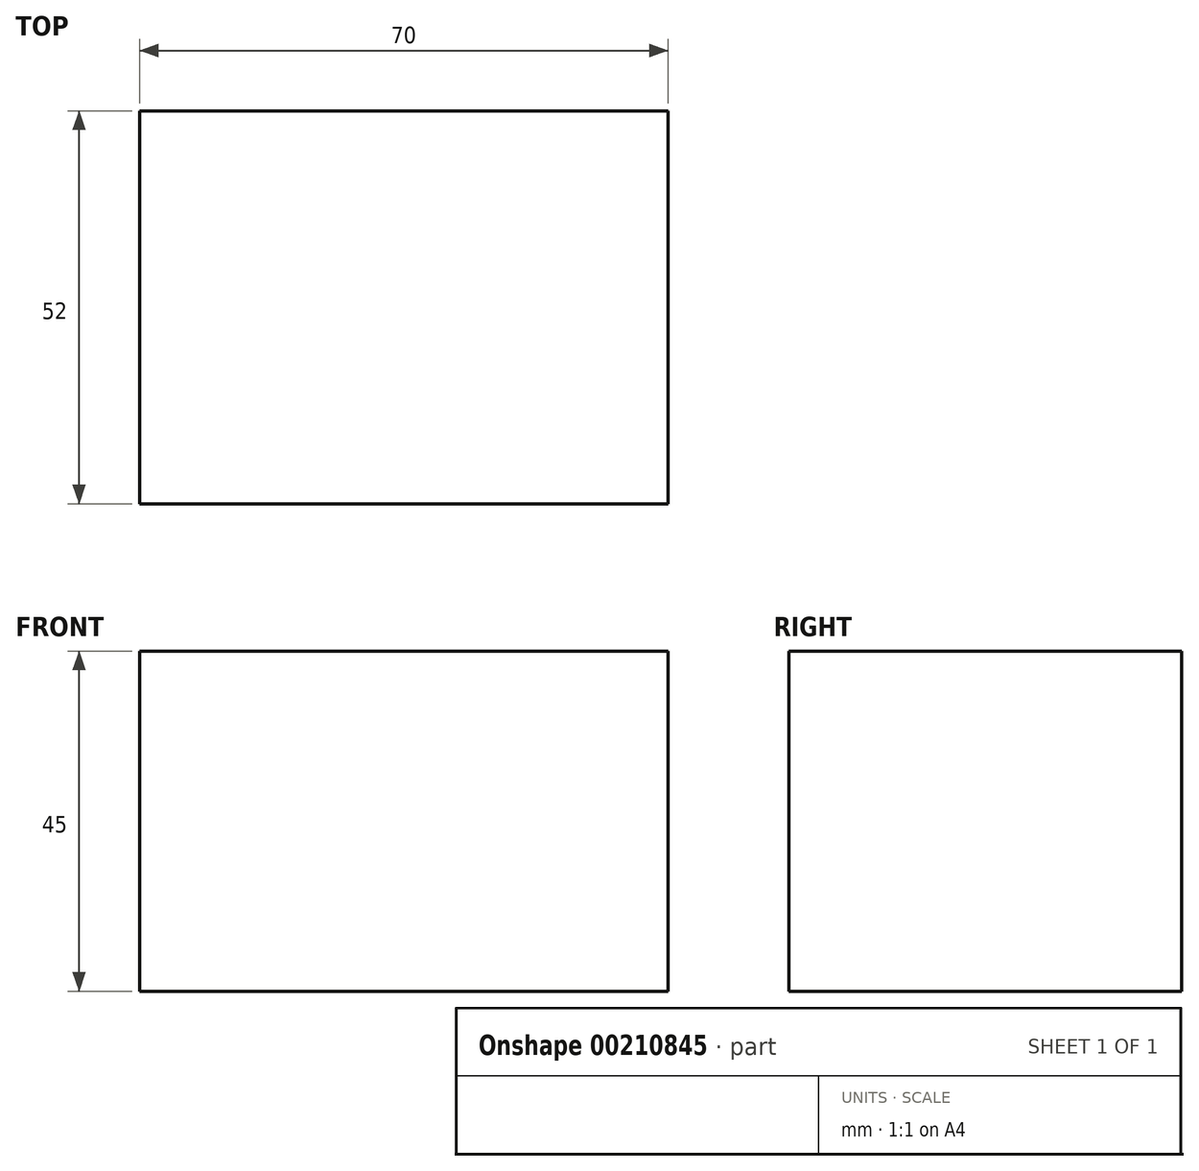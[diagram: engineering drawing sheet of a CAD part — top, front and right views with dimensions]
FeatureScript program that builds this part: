
annotation { "Feature Type Name" : "Feature", "Feature Type Description" : "" }
export const myFeature = defineFeature(function(context is Context, id is Id, definition is map)
    precondition{}
    {
        {
            var Q0;
            Q0=qCreatedBy(makeId("Top.planeOp"),FACE);
            var sketch = newSketch(context, id + "F0", { "sketchPlane" : qUnion([Q0])});
            skLineSegment(sketch, "E0", {"start": v(0, 0) * mm, "end": v(70, 0) * mm});
            skLineSegment(sketch, "E1.top", {"start": v(0, 52) * mm, "end": v(70, 52) * mm});
            skLineSegment(sketch, "E1.left", {"start": v(0, 0) * mm, "end": v(0, 52) * mm});
            skLineSegment(sketch, "E1.right", {"start": v(70, 0) * mm, "end": v(70, 52) * mm});
            skSolve(sketch);
        }
        {
            var Q0;
            Q0=makeQuery(id+"F0.imprint","IMPRINT",FACE,{"disambiguationData":[TD([[makeQuery(id+"F0.imprint","IMPRINT",EDGE,{"derivedFrom":sQuery(id+"F0.wireOp",EDGE,"E0")}),1.0]])]});
            extrude(context, id + "F1", {"entities" : qUnion([Q0]), "oppositeDirection" : true, "depth" : 45 * mm});
        }
    });
